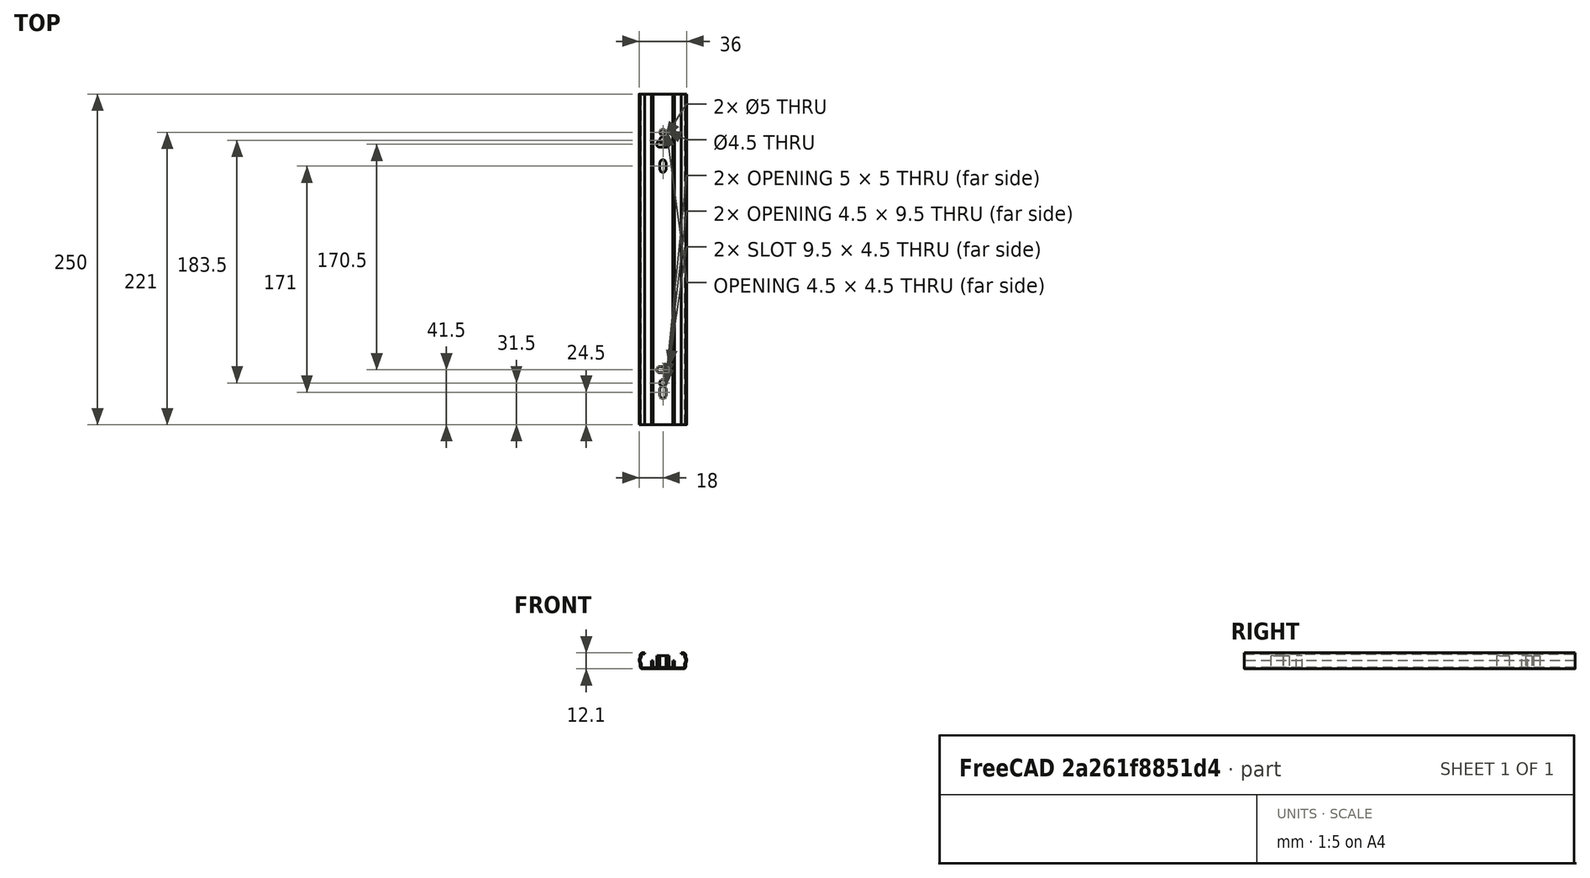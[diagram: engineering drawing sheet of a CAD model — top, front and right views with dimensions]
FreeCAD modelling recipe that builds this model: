
FCSTD DOCUMENT  (FreeCAD 0.22R37100 (Git))
Label: rails
License: All rights reserved
LicenseURL: http://en.wikipedia.org/wiki/All_rights_reserved
objects: Sketcher::SketchObject×4, PartDesign::CoordinateSystem×4, PartDesign::SubShapeBinder×3, Part::Mirroring×2, Part::FeaturePython×2, PartDesign::FeaturePython×2, Part::Extrusion×2, PartDesign::Boolean×2, App::Link×2, App::FeaturePython×2, PartDesign::Body×2, Part::Compound×1, Assembly::JointGroup×1, Assembly::AssemblyObject×1, App::Part×1
note: 24 computed .brp shape members not serialized (recipe doc carries the construction recipe); baked Part::Feature solids carry a one-line shape summary decoded from their .brp

FEATURE [Sketcher::SketchObject] Sketch
  FullyConstrained = true
  sketch-geometry (5):
    g0: LineSegment StartX=0 StartY=0 StartZ=0 EndX=17.25 EndY=0 EndZ=0
    g1: LineSegment StartX=17.25 StartY=12.1 StartZ=0 EndX=13.75 EndY=12.1 EndZ=0
    g2: LineSegment StartX=17.25 StartY=0 StartZ=0 EndX=17.25 EndY=4.16816 EndZ=0
    g3: LineSegment StartX=17.25 StartY=8.83184 StartZ=0 EndX=17.25 EndY=12.1 EndZ=0
    g4: ArcOfCircle CenterX=14 CenterY=6.5 CenterZ=0 NormalX=0 NormalY=0 NormalZ=1 AngleXU=0 Radius=4 StartAngle=5.66082 EndAngle=6.90555
  constraints (16):
    c: Coincident(g-1,g0)
    c: PointOnObject(g0,g-1)
    c: Coincident(g0,g2)
    c: DistanceX(g0) = 17.25
    c: DistanceY(g3) = 12.1
    c: Coincident(g1,g3)
    c: Horizontal(g1)
    c: Vertical(g2)
    c: Vertical(g3)
    c: Coincident(g4,g2)
    c: Coincident(g4,g3)
    c: Vertical(g0,g1)
    c: DistanceX(g1) = 13.75
    c: DistanceY(g4) = 6.5
    c: Radius(g4) = 4
    c: DistanceX(g4) = 14
FEATURE [Part::Mirroring] Part__Mirroring  label="Sketch (Mirror #1)"
  Base = (0,0,0)
  Normal = (1,0,0)
  Source = -> Sketch
FEATURE [Part::FeaturePython] Connect  # WARN: FeaturePython — macro-defined, semantics opaque (R4)
  Objects = -> [Sketch,Part__Mirroring]
  Tolerance = 0
FEATURE [PartDesign::SubShapeBinder] Binder
  BindCopyOnChange = 0
  BindMode = 0
  ClaimChildren = true
  Context = -> Body [Binder.]
  Fuse = false
  MakeFace = true
  OffsetFill = false
  OffsetIntersection = false
  OffsetJoinType = 0
  OffsetOpenResult = false
  PartialLoad = false
  Placement = pos=(0,0,0) rot=(0,0.707107,0.707107;3.14159rad)
  Relative = false
  Support = -> [Connect]
  _Version = 2
FEATURE [PartDesign::FeaturePython] BaseBend  # WARN: FeaturePython — macro-defined, semantics opaque (R4)
  BendSide = 1
  BendSketch = -> Binder
  MidPlane = false
  Reverse = false
  Suppressed = false
  length = 250
  radius = 1
  thickness = 0.8
FEATURE [Sketcher::SketchObject] Sketch001
  FullyConstrained = true
  sketch-geometry (2):
    g0: Circle CenterX=0 CenterY=31.5 CenterZ=0 NormalX=0 NormalY=0 NormalZ=1 AngleXU=0 Radius=2.5
    g1: Circle CenterX=0 CenterY=215 CenterZ=0 NormalX=0 NormalY=0 NormalZ=1 AngleXU=0 Radius=2.5
  constraints (6):
    c: PointOnObject(g0,g-2)
    c: PointOnObject(g1,g-2)
    c: DistanceY(g0) = 31.5
    c: Equal(g0,g1)
    c: Diameter(g0) = 5
    c: DistanceY(g1) = 215
FEATURE [Part::Extrusion] Extrude
  Base = -> Sketch001
  Dir = (0,0,1)
  DirMode = 2
  FaceMakerClass = Part::FaceMakerBullseye
  LengthFwd = 10
  LengthRev = 0
  Solid = true
  Symmetric = false
FEATURE [Part::Compound] Compound
  Links = -> [Extrude]
FEATURE [PartDesign::Boolean] Boolean
  BaseFeature = -> BaseBend
  Group = -> [Compound]
  Refine = true
  Suppressed = false
  Type = 1
  UsePlacement = true
FEATURE [Sketcher::SketchObject] Sketch002
  FullyConstrained = true
  sketch-geometry (2):
    g0: LineSegment StartX=0 StartY=0 StartZ=0 EndX=8.6 EndY=0 EndZ=0
    g1: LineSegment StartX=8.6 StartY=0 StartZ=0 EndX=8.6 EndY=6.3 EndZ=0
  constraints (6):
    c: Coincident(g-1,g0)
    c: PointOnObject(g0,g-1)
    c: Coincident(g0,g1)
    c: Vertical(g1)
    c: DistanceX(g1) = 8.6
    c: DistanceY(g1) = 6.3
FEATURE [Part::Mirroring] Part__Mirroring001  label="Sketch002 (Mirror #2)"
  Base = (0,0,0)
  Normal = (1,0,0)
  Source = -> Sketch002
FEATURE [Part::FeaturePython] Connect001  # WARN: FeaturePython — macro-defined, semantics opaque (R4)
  Objects = -> [Sketch002,Part__Mirroring001]
  Tolerance = 0
FEATURE [PartDesign::SubShapeBinder] Binder001
  BindCopyOnChange = 0
  BindMode = 0
  ClaimChildren = true
  Context = -> Body001 [Binder001.]
  Fuse = false
  MakeFace = true
  OffsetFill = false
  OffsetIntersection = false
  OffsetJoinType = 0
  OffsetOpenResult = false
  PartialLoad = false
  Placement = pos=(0,0,0) rot=(1,0,0;1.5708rad)
  Relative = false
  Support = -> [Connect001]
  _Version = 2
FEATURE [PartDesign::FeaturePython] BaseBend001  # WARN: FeaturePython — macro-defined, semantics opaque (R4)
  BendSide = 1
  BendSketch = -> Binder001
  MidPlane = false
  Reverse = true
  Suppressed = false
  length = 250
  radius = 1
  thickness = 1
FEATURE [Sketcher::SketchObject] Sketch003
  FullyConstrained = true
  sketch-geometry (19):
    g0: ArcOfCircle CenterX=0 CenterY=22 CenterZ=0 NormalX=0 NormalY=0 NormalZ=1 AngleXU=0 Radius=2.25 StartAngle=3.14159 EndAngle=6.28319
    g1: ArcOfCircle CenterX=2e-16 CenterY=27 CenterZ=0 NormalX=0 NormalY=0 NormalZ=1 AngleXU=0 Radius=2.25 StartAngle=0 EndAngle=3.14159
    g2: LineSegment StartX=-2.25 StartY=22 StartZ=0 EndX=-2.25 EndY=27 EndZ=0
    g3: LineSegment StartX=2.25 StartY=22 StartZ=0 EndX=2.25 EndY=27 EndZ=0
    g4: ArcOfCircle CenterX=-2.5 CenterY=41.5 CenterZ=0 NormalX=0 NormalY=0 NormalZ=1 AngleXU=0 Radius=2.25 StartAngle=1.5708 EndAngle=4.71239
    g5: ArcOfCircle CenterX=2.5 CenterY=41.5 CenterZ=0 NormalX=0 NormalY=0 NormalZ=1 AngleXU=0 Radius=2.25 StartAngle=4.71239 EndAngle=7.85398
    g6: LineSegment StartX=-2.5 StartY=43.75 StartZ=0 EndX=2.5 EndY=43.75 EndZ=0
    g7: LineSegment StartX=-2.5 StartY=39.25 StartZ=0 EndX=2.5 EndY=39.25 EndZ=0
    g8: ArcOfCircle CenterX=0 CenterY=193 CenterZ=0 NormalX=0 NormalY=0 NormalZ=1 AngleXU=0 Radius=2.25 StartAngle=3.14159 EndAngle=6.28319
    g9: ArcOfCircle CenterX=1e-16 CenterY=198 CenterZ=0 NormalX=0 NormalY=0 NormalZ=1 AngleXU=0 Radius=2.25 StartAngle=3.5e-15 EndAngle=3.14159
    g10: LineSegment StartX=-2.25 StartY=193 StartZ=0 EndX=-2.25 EndY=198 EndZ=0
    g11: LineSegment StartX=2.25 StartY=193 StartZ=0 EndX=2.25 EndY=198 EndZ=0
    g12: ArcOfCircle CenterX=-2.5 CenterY=212 CenterZ=0 NormalX=0 NormalY=0 NormalZ=1 AngleXU=0 Radius=2.25 StartAngle=1.5708 EndAngle=4.71239
    g13: ArcOfCircle CenterX=2.5 CenterY=212 CenterZ=0 NormalX=0 NormalY=0 NormalZ=1 AngleXU=0 Radius=2.25 StartAngle=4.71239 EndAngle=7.85398
    g14: LineSegment StartX=-2.5 StartY=214.25 StartZ=0 EndX=2.5 EndY=214.25 EndZ=0
    g15: LineSegment StartX=-2.5 StartY=209.75 StartZ=0 EndX=2.5 EndY=209.75 EndZ=0
    g16: Circle CenterX=0 CenterY=221 CenterZ=0 NormalX=0 NormalY=0 NormalZ=1 AngleXU=0 Radius=2.25
    g17: GeomPoint X=-4.75 Y=41.5 Z=0
    g18: GeomPoint X=4.75 Y=41.5 Z=0
  constraints (45):
    c: Tangent(g0,g2) = 1.5708
    c: Tangent(g0,g3) = -1.5708
    c: Tangent(g1,g2) = 1.5708
    c: Tangent(g1,g3) = -1.5708
    c: Equal(g0,g1)
    c: Vertical(g3)
    c: PointOnObject(g0,g-2)
    c: Tangent(g4,g6) = 1.5708
    c: Tangent(g4,g7) = -1.5708
    c: Tangent(g5,g6) = 1.5708
    c: Tangent(g5,g7) = -1.5708
    c: Equal(g4,g5)
    c: Tangent(g8,g10) = 1.5708
    c: Tangent(g8,g11) = -1.5708
    c: Tangent(g9,g10) = 1.5708
    c: Tangent(g9,g11) = -1.5708
    c: Equal(g8,g9)
    c: Vertical(g11)
    c: PointOnObject(g8,g-2)
    c: Tangent(g12,g14) = 1.5708
    c: Tangent(g12,g15) = -1.5708
    c: Tangent(g13,g14) = 1.5708
    c: Tangent(g13,g15) = -1.5708
    c: Equal(g12,g13)
    c: PointOnObject(g16,g-2)
    c: Symmetric(g5,g4,g-2)
    c: Symmetric(g13,g12,g-2)
    c: Equal(g16,g13)
    c: Equal(g13,g9)
    c: Equal(g9,g5)
    c: Equal(g5,g1)
    c: Diameter(g16) = 4.5
    c: PointOnObject(g17,g4)
    c: PointOnObject(g18,g5)
    c: Horizontal(g18,g5)
    c: Horizontal(g5,g17)
    c: DistanceX(g17,g18) = 9.5
    c: Equal(g3,g7)
    c: Equal(g7,g11)
    c: Equal(g11,g15)
    c: DistanceY(g1) = 27
    c: DistanceY(g5) = 41.5
    c: DistanceY(g9) = 198
    c: DistanceY(g13) = 212
    c: DistanceY(g16) = 221
FEATURE [PartDesign::SubShapeBinder] Binder002
  BindCopyOnChange = 0
  BindMode = 0
  ClaimChildren = true
  Fuse = false
  MakeFace = true
  OffsetFill = false
  OffsetIntersection = false
  OffsetJoinType = 0
  OffsetOpenResult = false
  PartialLoad = false
  Relative = false
  Support = -> [Sketch003]
  _Version = 2
FEATURE [Part::Extrusion] Extrude001
  Base = -> Binder002
  Dir = (0,0,1)
  DirMode = 2
  FaceMakerClass = Part::FaceMakerBullseye
  LengthFwd = 10
  LengthRev = 0
  Solid = false
  Symmetric = false
FEATURE [PartDesign::Boolean] Boolean001
  BaseFeature = -> BaseBend001
  Group = -> [Extrude001]
  Refine = true
  Suppressed = false
  Type = 1
  UsePlacement = true
FEATURE [App::Link] Body002
  LinkedObject = -> Body
FEATURE [App::FeaturePython] GroundedJoint  # Assembly grounded joint (typed FeaturePython)
  ObjectToGround = -> Body002
FEATURE [App::Link] Body003
  LinkPlacement = pos=(0,0,12) rot=(0,1,0;3.14159rad)
  LinkedObject = -> Body001
  Placement = pos=(0,0,12) rot=(0,1,0;3.14159rad)
FEATURE [PartDesign::CoordinateSystem] Local_CS
  AttacherType = Attacher::AttachEngine3D
  AttachmentSupport = -> [XY_Plane]
  MapMode = 5
FEATURE [PartDesign::CoordinateSystem] Local_CS001
  AttacherType = Attacher::AttachEngine3D
  AttachmentSupport = -> [XY_Plane001]
  MapMode = 5
FEATURE [PartDesign::Body] Body001
  Group = -> [Binder001,BaseBend001,Boolean001,Local_CS001]
  Origin = -> Origin001
  Tip = -> Boolean001
FEATURE [PartDesign::CoordinateSystem] Local_CS002
  AttacherType = Attacher::AttachEngine3D
  AttachmentOffset = pos=(0,0,12) rot=(0,1,0;3.14159rad)
  AttachmentSupport = -> [XY_Plane]
  MapMode = 5
  Placement = pos=(0,0,12) rot=(0,1,0;3.14159rad)
FEATURE [PartDesign::Body] Body
  Group = -> [Binder,BaseBend,Boolean,Local_CS,Local_CS002]
  Origin = -> Origin
  Tip = -> Boolean
FEATURE [App::FeaturePython] Slider  # Assembly joint (typed FeaturePython)
  Activated = true
  AngleMax = 0
  AngleMin = 0
  Detach1 = false
  Detach2 = false
  Distance = 0
  Distance2 = 0
  EnableAngleMax = false
  EnableAngleMin = false
  EnableLengthMax = false
  EnableLengthMin = false
  EnableLimits = true
  JointType = 3 (Slider)
  LengthMax = 250
  LengthMin = 0
  Offset = (0,0,0)
  Rotation = 0
FEATURE [Assembly::JointGroup] Joints
  Group = -> [GroundedJoint,Slider]
FEATURE [Assembly::AssemblyObject] Assembly  label="rail_Assembly"
  Group = -> [Joints,Body002,GroundedJoint,Body003,Slider]
  Origin = -> Origin002
  Type = Assembly
FEATURE [PartDesign::CoordinateSystem] LCS_1  label="rail_LCS"
  AttacherType = Attacher::AttachEngine3D
  AttachmentSupport = -> [XY_Plane003]
  MapMode = 5
FEATURE [App::Part] Part  label="rail_Part"
  Group = -> [Assembly,LCS_1]
  Origin = -> Origin003
